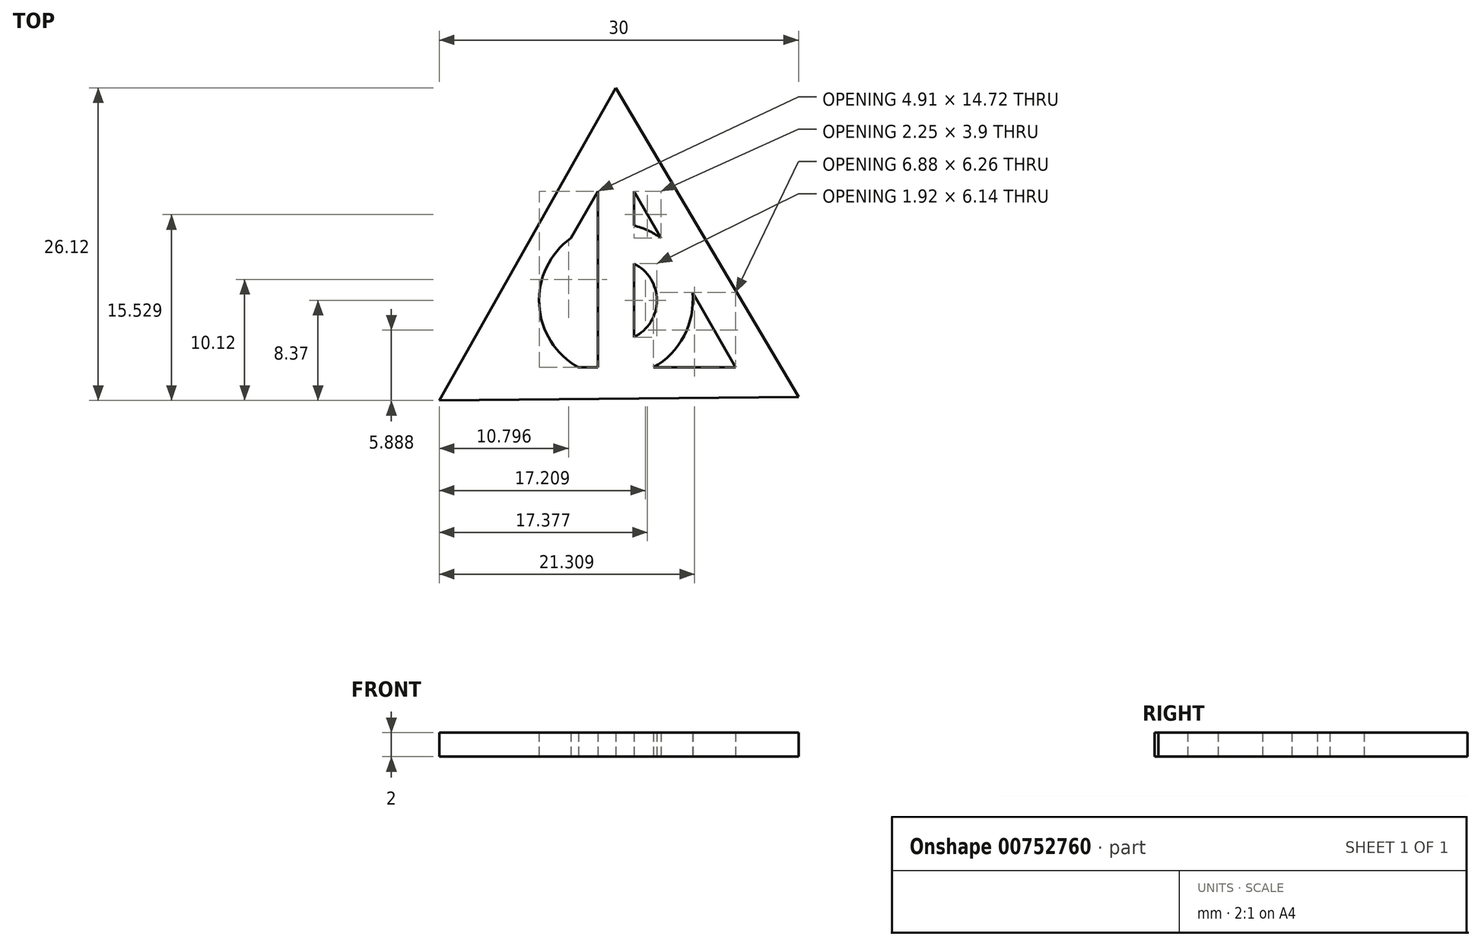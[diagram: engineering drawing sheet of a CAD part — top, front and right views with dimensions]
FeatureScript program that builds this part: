
annotation { "Feature Type Name" : "Feature", "Feature Type Description" : "" }
export const myFeature = defineFeature(function(context is Context, id is Id, definition is map)
    precondition{}
    {
        {
            var Q0;
            Q0=qCreatedBy(makeId("Top.planeOp"),FACE);
            var sketch = newSketch(context, id + "F0", { "sketchPlane" : qUnion([Q0])});
            skLineSegment(sketch, "E0", {"start": v(-15.25, 56.89) * mm, "end": v(-25.25, 39.57) * mm});
            skLineSegment(sketch, "E1", {"start": v(-25.25, 39.57) * mm, "end": v(-5.25, 39.57) * mm});
            skLineSegment(sketch, "E2", {"start": v(-5.25, 39.57) * mm, "end": v(-15.25, 56.89) * mm});
            skLineSegment(sketch, "E3", {"start": v(-15.25, 62.93) * mm, "end": v(-30, 36.8) * mm});
            skLineSegment(sketch, "E4", {"start": v(-30, 36.8) * mm, "end": v(0, 37.1) * mm});
            skLineSegment(sketch, "E5", {"start": v(0, 37.1) * mm, "end": v(-15.25, 62.93) * mm});
            skLineSegment(sketch, "E6", {"start": v(-16.75, 54.3) * mm, "end": v(-16.75, 39.57) * mm});
            skLineSegment(sketch, "E7", {"start": v(-13.75, 54.3) * mm, "end": v(-13.75, 39.57) * mm});
            skCircle(sketch, "E8", {"center": v(-15.25, 45.18) * mm, "radius": 6.42 * mm});
            skCircle(sketch, "E9", {"center": v(-15.25, 45.18) * mm, "radius": 3.42 * mm});
            skSolve(sketch);
        }
        {
            var Q0;
            Q0=makeQuery(id+"F0.imprint","IMPRINT",FACE,{"disambiguationData":[TD([[makeQuery(id+"F0.imprint","IMPRINT",EDGE,{"derivedFrom":sQuery(id+"F0.wireOp",EDGE,"E3")}),1.0]])]});
            var Q1;
            {var subQ0=sQuery(id+"F0.wireOp",EDGE,"E7");var subQ1=sQuery(id+"F0.wireOp",EDGE,"E1");var subQ2=makeQuery(id+"F0.imprint","INTERSECT",VERTEX,{"derivedFrom":[subQ1,subQ0]});Q1=makeQuery(id+"F0.imprint","IMPRINT",FACE,{"disambiguationData":[TD([[makeQuery(id+"F0.imprint","IMPRINT",EDGE,{"disambiguationData":[TD([[subQ2,-1.0]])],"derivedFrom":subQ1}),1.0]])]});}
            var Q2;
            {var subQ5=sQuery(id+"F0.wireOp",EDGE,"E8");var subQ9=sQuery(id+"F0.wireOp",EDGE,"E0");var subQ11=makeQuery(id+"F0.imprint","INTERSECT",VERTEX,{"disambiguationData":[OD(0.0)],"derivedFrom":[subQ9,subQ5]});Q2=makeQuery(id+"F0.imprint","IMPRINT",FACE,{"disambiguationData":[TD([[makeQuery(id+"F0.imprint","IMPRINT",EDGE,{"disambiguationData":[TD([[subQ11,-1.0]])],"derivedFrom":subQ9}),1.0]])]});}
            var Q3;
            {var subQ0=sQuery(id+"F0.wireOp",EDGE,"E1");var subQ1=makeQuery(id+"F0.imprint","INTERSECT",VERTEX,{"derivedFrom":[subQ0,sQuery(id+"F0.wireOp",EDGE,"E6")]});Q3=makeQuery(id+"F0.imprint","IMPRINT",FACE,{"disambiguationData":[TD([[makeQuery(id+"F0.imprint","IMPRINT",EDGE,{"disambiguationData":[TD([[subQ1,1.0]])],"derivedFrom":subQ0}),-1.0]])]});}
            var Q4;
            {var subQ0=sQuery(id+"F0.wireOp",EDGE,"E8");var subQ1=sQuery(id+"F0.wireOp",EDGE,"E6");var subQ2=makeQuery(id+"F0.imprint","INTERSECT",VERTEX,{"derivedFrom":[subQ1,subQ0]});Q4=makeQuery(id+"F0.imprint","IMPRINT",FACE,{"disambiguationData":[TD([[makeQuery(id+"F0.imprint","IMPRINT",EDGE,{"disambiguationData":[TD([[subQ2,-1.0]])],"derivedFrom":subQ1}),1.0]])]});}
            var Q5;
            {var subQ0=sQuery(id+"F0.wireOp",EDGE,"E9");var subQ1=sQuery(id+"F0.wireOp",EDGE,"E6");var subQ2=makeQuery(id+"F0.imprint","INTERSECT",VERTEX,{"disambiguationData":[OD(0.0)],"derivedFrom":[subQ1,subQ0]});Q5=makeQuery(id+"F0.imprint","IMPRINT",FACE,{"disambiguationData":[TD([[makeQuery(id+"F0.imprint","IMPRINT",EDGE,{"disambiguationData":[TD([[subQ2,-1.0]])],"derivedFrom":subQ1}),1.0]])]});}
            var Q6;
            {var subQ1=sQuery(id+"F0.wireOp",EDGE,"E0");var subQ5=sQuery(id+"F0.wireOp",EDGE,"E2");var subQ6=makeQuery(id+"F0.imprint","INTERSECT",VERTEX,{"derivedFrom":[subQ1,subQ5]});Q6=makeQuery(id+"F0.imprint","IMPRINT",FACE,{"disambiguationData":[TD([[makeQuery(id+"F0.imprint","IMPRINT",EDGE,{"disambiguationData":[TD([[subQ6,-1.0]])],"derivedFrom":subQ1}),1.0]])]});}
            var Q7;
            {var subQ0=sQuery(id+"F0.wireOp",EDGE,"E8");var subQ1=sQuery(id+"F0.wireOp",EDGE,"E0");var subQ2=makeQuery(id+"F0.imprint","INTERSECT",VERTEX,{"disambiguationData":[OD(0.0)],"derivedFrom":[subQ1,subQ0]});Q7=makeQuery(id+"F0.imprint","IMPRINT",FACE,{"disambiguationData":[TD([[makeQuery(id+"F0.imprint","IMPRINT",EDGE,{"disambiguationData":[TD([[subQ2,-1.0]])],"derivedFrom":subQ1}),-1.0]])]});}
            var Q8;
            {var subQ0=sQuery(id+"F0.wireOp",EDGE,"E8");var subQ1=sQuery(id+"F0.wireOp",EDGE,"E2");var subQ2=makeQuery(id+"F0.imprint","INTERSECT",VERTEX,{"disambiguationData":[OD(0.0)],"derivedFrom":[subQ1,subQ0]});Q8=makeQuery(id+"F0.imprint","IMPRINT",FACE,{"disambiguationData":[TD([[makeQuery(id+"F0.imprint","IMPRINT",EDGE,{"disambiguationData":[TD([[subQ2,-1.0]])],"derivedFrom":subQ1}),-1.0]])]});}
            var Q9;
            {var subQ0=sQuery(id+"F0.wireOp",EDGE,"E6");var subQ1=sQuery(id+"F0.wireOp",EDGE,"E1");var subQ2=makeQuery(id+"F0.imprint","INTERSECT",VERTEX,{"derivedFrom":[subQ1,subQ0]});Q9=makeQuery(id+"F0.imprint","IMPRINT",FACE,{"disambiguationData":[TD([[makeQuery(id+"F0.imprint","IMPRINT",EDGE,{"disambiguationData":[TD([[subQ2,-1.0]])],"derivedFrom":subQ1}),1.0]])]});}
            extrude(context, id + "F1", {"entities" : qUnion([Q0, Q1, Q2, Q3, Q4, Q5, Q6, Q7, Q8, Q9]), "depth" : 2 * mm, "offsetDistance" : 25 * mm});
        }
    });
